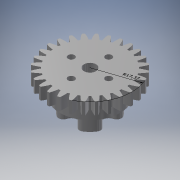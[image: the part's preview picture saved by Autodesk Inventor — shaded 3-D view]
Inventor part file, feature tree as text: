
AUTODESK INVENTOR PART (.ipt)
format: ipt  version: 2018 (Build 220112000, 112)  size: 330,752 bytes
history: native  units: mm (DEFAULTED — no unit token found)
features: sketch x7, extrude x6, other x5, plane x3, pattern_circular x1, fillet x1
ambient origin geometry x8: Origin, YZ Plane, XZ Plane, XY Plane, X Axis, Y Axis, Z Axis, Center Point
bodies: Solid1 (feature_tree)
feature tree (23):
  other  "Annotations"
  extrude  "Extrusion1"  Depth=5.0mm TaperAngle=0.0deg
  plane  "Work Plane2"
  plane  "Work Plane8"
  plane  "Work Plane9"
  other  "Engrenage cylindrique"
  extrude  "Extrusion4"  Depth=10.0mm TaperAngle=0.0deg
  extrude  "Extrusion5"  Depth=17.374537mm
  extrude  "Extrusion2"  Depth=17.374537mm TaperAngle=0.0deg
  extrude  "Extrusion3"  TaperAngle=0.0deg  [1 undecoded]
  extrude  "Extrusion6"  TaperAngle=0.0deg  [1 undecoded]
  pattern_circular  "Réseau circulaire1"  [2 undecoded]
  fillet  "Congé1"  Radius=32.0mm
  sketch  "Sketch1"  dims[d0=34.749074mm d1=5.0mm d2=0.0mm]
  sketch  "Sketch2"  dims[d3=31.438596mm d4=10.0mm d5=0.0mm d16=32.0mm d17=0.0mm d34=1.121997mm d39=0.0mm d41=0.0mm d43=32.0mm d46=32.0mm d47=0.0mm d48=0.0mm d49=5.0mm d51=0.0mm d52=17.0mm d53=2.7mm d54=7.75mm d55=10.0mm d56=0.0mm d57=40.0mm d58=360.0deg d60=20.0mm d61=25.0mm d62=5.0mm d63=0.0mm d64=20.0mm d65=11.0mm d66=0.0mm d67=12.0mm d68=0.0mm d69=5.0mm d70=11.0mm d71=0.0mm d72=2.0mm d73=3.230448mm d74=17.374537mm]
  other  "Srf1"
  sketch  "Esquisse4"
  sketch  "Esquisse5"
  sketch  "Esquisse6"
  sketch  "Esquisse7"
  other  "Diamètre primitif"
  sketch  "Esquisse3"
  other  "Cote de rayon 1"
note: 4 required parameter values undecoded (feature->parameter linkage not recoverable at this tier; creation-order binding heuristic only, values carry confidence <= 0.55)
